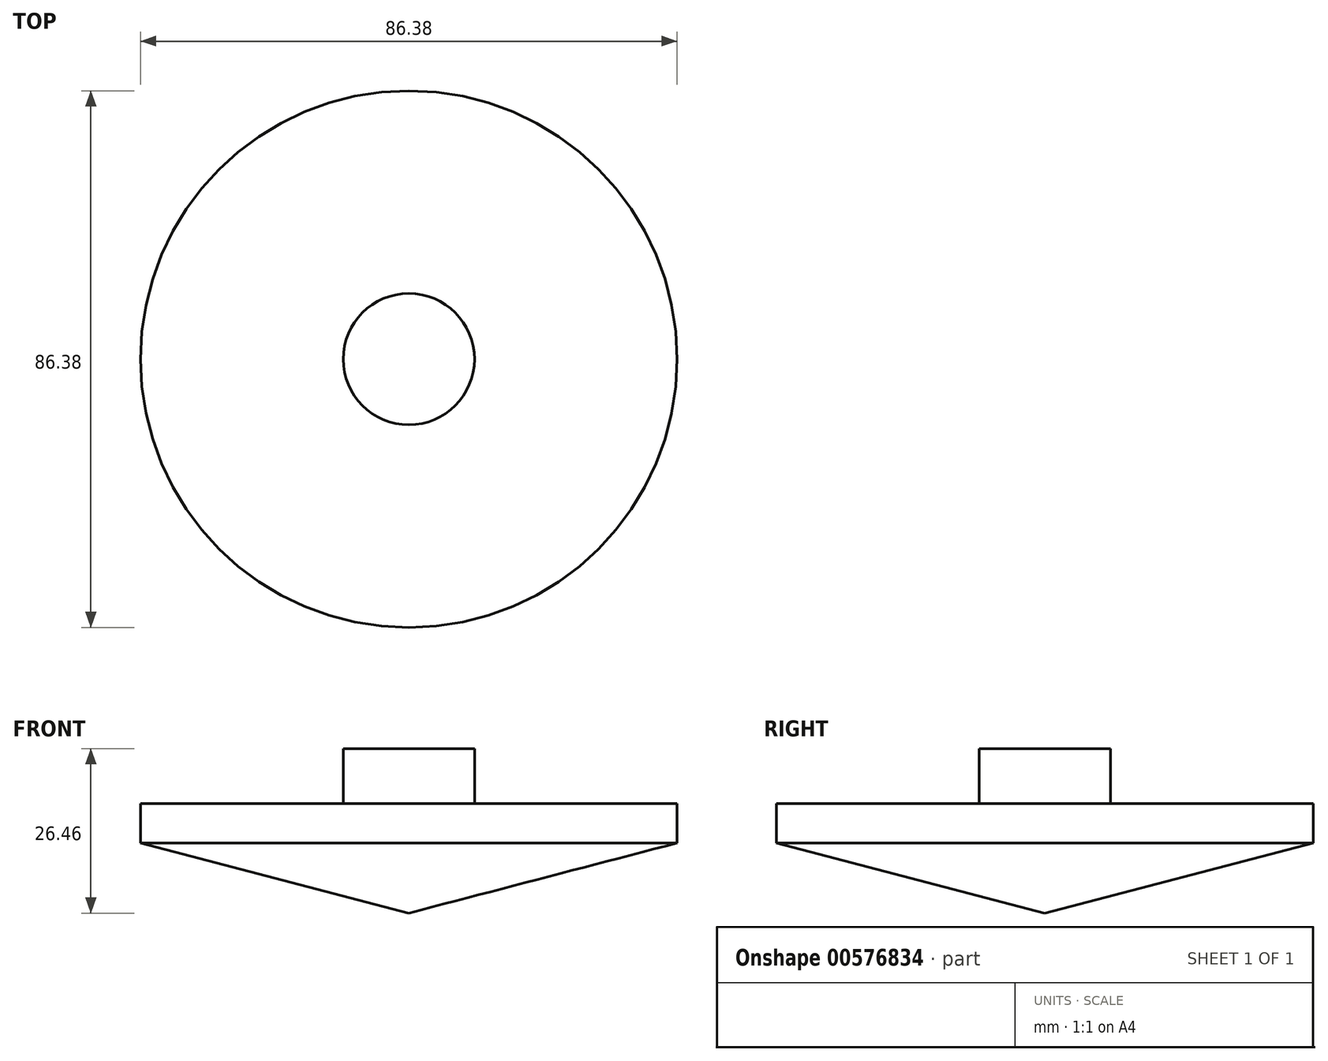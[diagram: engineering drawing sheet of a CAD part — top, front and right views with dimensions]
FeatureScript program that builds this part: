
annotation { "Feature Type Name" : "Feature", "Feature Type Description" : "" }
export const myFeature = defineFeature(function(context is Context, id is Id, definition is map)
    precondition{}
    {
        {
            var Q0;
            Q0=qCreatedBy(makeId("Front.planeOp"),FACE);
            var sketch = newSketch(context, id + "F0", { "sketchPlane" : qUnion([Q0])});
            skLineSegment(sketch, "E0", {"start": v(0, 0) * mm, "end": v(43.2, 11.28) * mm});
            skLineSegment(sketch, "E1", {"start": v(43.2, 11.28) * mm, "end": v(43.2, 17.6) * mm});
            skLineSegment(sketch, "E2", {"start": v(43.2, 17.6) * mm, "end": v(10.57, 17.6) * mm});
            skLineSegment(sketch, "E3", {"start": v(10.57, 17.6) * mm, "end": v(10.57, 26.46) * mm});
            skLineSegment(sketch, "E4", {"start": v(10.57, 26.46) * mm, "end": v(0, 26.46) * mm});
            skLineSegment(sketch, "E5", {"start": v(0, 26.46) * mm, "end": v(0, 0) * mm});
            skSolve(sketch);
        }
        {
            var Q0;
            Q0=makeQuery(id+"F0.imprint","IMPRINT",FACE,{"disambiguationData":[TD([[makeQuery(id+"F0.imprint","IMPRINT",EDGE,{"derivedFrom":sQuery(id+"F0.wireOp",EDGE,"E0")}),1.0]])]});
            var Q1;
            Q1=sQuery(id+"F0.wireOp",EDGE,"E5");
            revolve(context, id + "F1", {"entities" : qUnion([Q0]), "axis" : qUnion([Q1]), "revolveType" : RevolveType.FULL});
        }
    });
